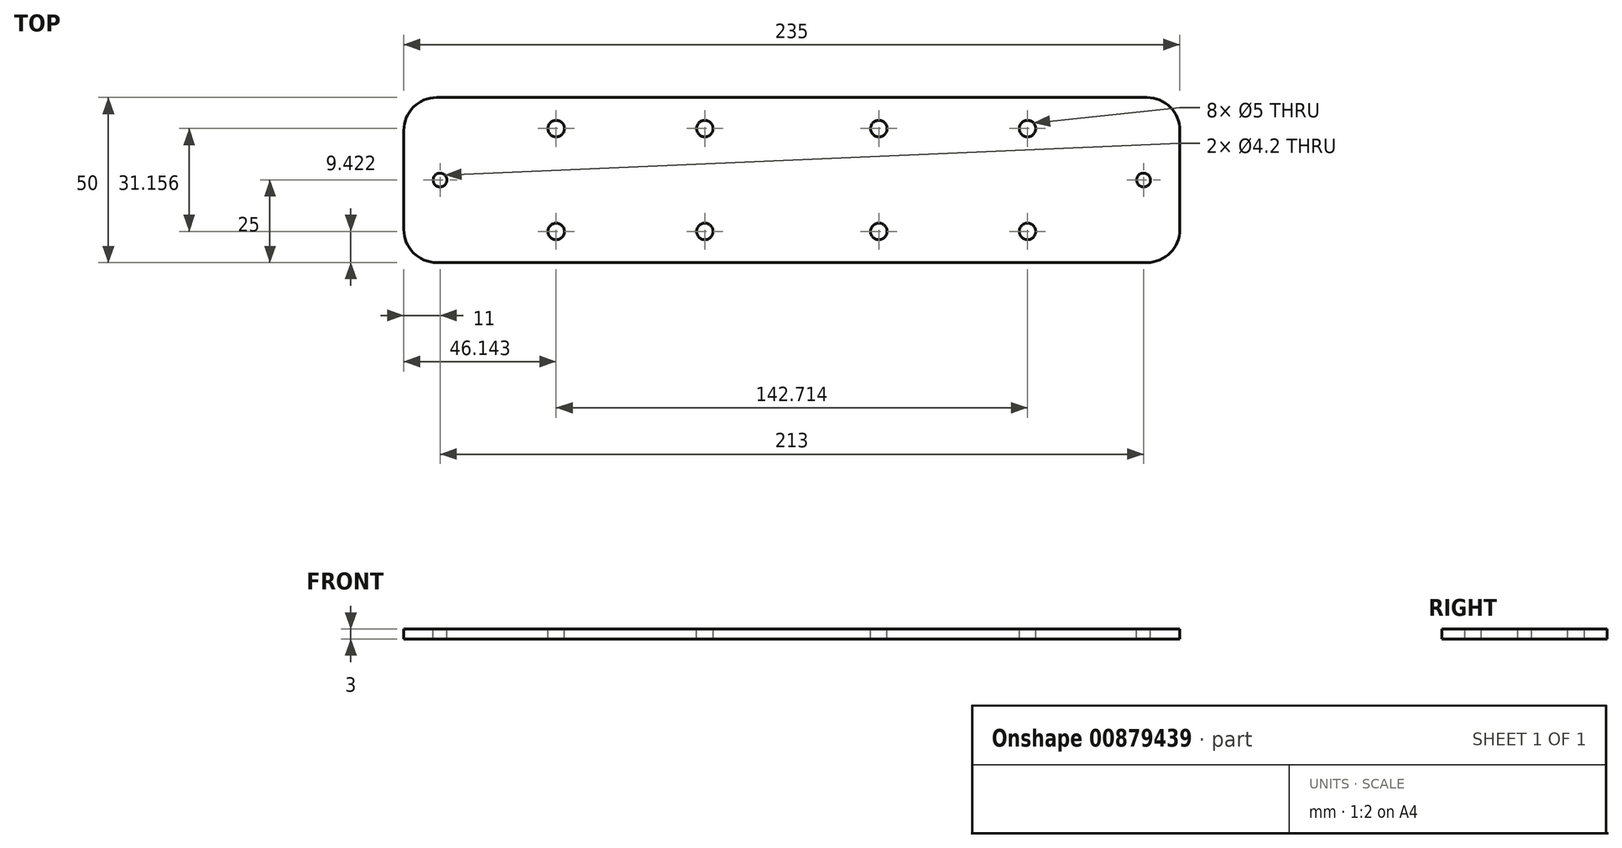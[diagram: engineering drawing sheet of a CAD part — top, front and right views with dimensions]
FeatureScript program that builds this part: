
annotation { "Feature Type Name" : "Feature", "Feature Type Description" : "" }
export const myFeature = defineFeature(function(context is Context, id is Id, definition is map)
    precondition{}
    {
        {
            var Q0;
            Q0=qCreatedBy(makeId("Top.planeOp"),FACE);
            var sketch = newSketch(context, id + "F0", { "sketchPlane" : qUnion([Q0])});
            skLineSegment(sketch, "E0.bottom", {"start": v(117.5, -25) * mm, "end": v(-117.5, -25) * mm});
            skLineSegment(sketch, "E0.top", {"start": v(117.5, 25) * mm, "end": v(-117.5, 25) * mm});
            skLineSegment(sketch, "E0.left", {"start": v(117.5, -25) * mm, "end": v(117.5, 25) * mm});
            skLineSegment(sketch, "E0.right", {"start": v(-117.5, -25) * mm, "end": v(-117.5, 25) * mm});
            skPoint(sketch, "E0.middle", {"position": v(0, 0) * mm});
            skCircle(sketch, "E1", {"center": v(-106.5, 0) * mm, "radius": 2.1 * mm});
            skCircle(sketch, "E2.MirrorC", {"center": v(106.5, 0) * mm, "radius": 2.1 * mm});
            skSolve(sketch);
        }
        {
            var Q0;
            Q0 = qSketchRegion(id + "F0", true);
            extrude(context, id + "F1", {"entities" : qUnion([Q0]), "oppositeDirection" : true, "depth" : 3 * mm, "offsetDistance" : 25 * mm});
        }
        {
            var Q0;
            Q0=makeQuery(id+"F1.opExtrude","SWEPT_EDGE",EDGE,{"disambiguationData":[OSD([sQuery(id+"F0.wireOp",EDGE,"E0.top"),sQuery(id+"F0.wireOp",EDGE,"E0.left")])]});
            var Q1;
            Q1=makeQuery(id+"F1.opExtrude","SWEPT_EDGE",EDGE,{"disambiguationData":[OSD([sQuery(id+"F0.wireOp",EDGE,"E0.bottom"),sQuery(id+"F0.wireOp",EDGE,"E0.left")])]});
            var Q2;
            Q2=makeQuery(id+"F1.opExtrude","SWEPT_EDGE",EDGE,{"disambiguationData":[OSD([sQuery(id+"F0.wireOp",EDGE,"E0.bottom"),sQuery(id+"F0.wireOp",EDGE,"E0.right")])]});
            var Q3;
            Q3=makeQuery(id+"F1.opExtrude","SWEPT_EDGE",EDGE,{"disambiguationData":[OSD([sQuery(id+"F0.wireOp",EDGE,"E0.top"),sQuery(id+"F0.wireOp",EDGE,"E0.right")])]});
            fillet(context, id + "F2", {"entities" : qUnion([Q0, Q1, Q2, Q3]), "radius" : 10 * mm, "tangentPropagation" : true, "allowEdgeOverflow" : false});
        }
        {
            var Q0;
            Q0=makeQuery(id+"F1.opExtrude","CAP_FACE",FACE,{"disambiguationData":[OSD([sQuery(id+"F0.wireOp",EDGE,"E0.bottom"),sQuery(id+"F0.wireOp",EDGE,"E0.top"),sQuery(id+"F0.wireOp",EDGE,"E0.left"),sQuery(id+"F0.wireOp",EDGE,"E0.right"),sQuery(id+"F0.wireOp",EDGE,"E1"),sQuery(id+"F0.wireOp",EDGE,"E2.MirrorC")])],"isStart":true});
            var sketch = newSketch(context, id + "F3", { "sketchPlane" : qUnion([Q0])});
            skCircle(sketch, "E3", {"center": v(-71.36, 15.58) * mm, "radius": 2.5 * mm});
            skCircle(sketch, "E4", {"center": v(-26.35, 15.58) * mm, "radius": 2.5 * mm});
            skCircle(sketch, "E5.MirrorC", {"center": v(71.36, 15.58) * mm, "radius": 2.5 * mm});
            skCircle(sketch, "E6.MirrorC", {"center": v(26.35, 15.58) * mm, "radius": 2.5 * mm});
            skCircle(sketch, "E7.MirrorC", {"center": v(71.36, -15.58) * mm, "radius": 2.5 * mm});
            skCircle(sketch, "E8.MirrorC", {"center": v(-26.35, -15.58) * mm, "radius": 2.5 * mm});
            skCircle(sketch, "E9.MirrorC", {"center": v(-71.36, -15.58) * mm, "radius": 2.5 * mm});
            skCircle(sketch, "E10.MirrorC", {"center": v(26.35, -15.58) * mm, "radius": 2.5 * mm});
            skSolve(sketch);
        }
        {
            var Q0;
            Q0 = qSketchRegion(id + "F3", true);
            extrude(context, id + "F4", {"entities" : qUnion([Q0]), "operationType" : NewBodyOperationType.REMOVE, "endBound" : BoundingType.THROUGH_ALL, "oppositeDirection" : true, "depth" : 25 * mm, "offsetDistance" : 25 * mm});
        }
    });
